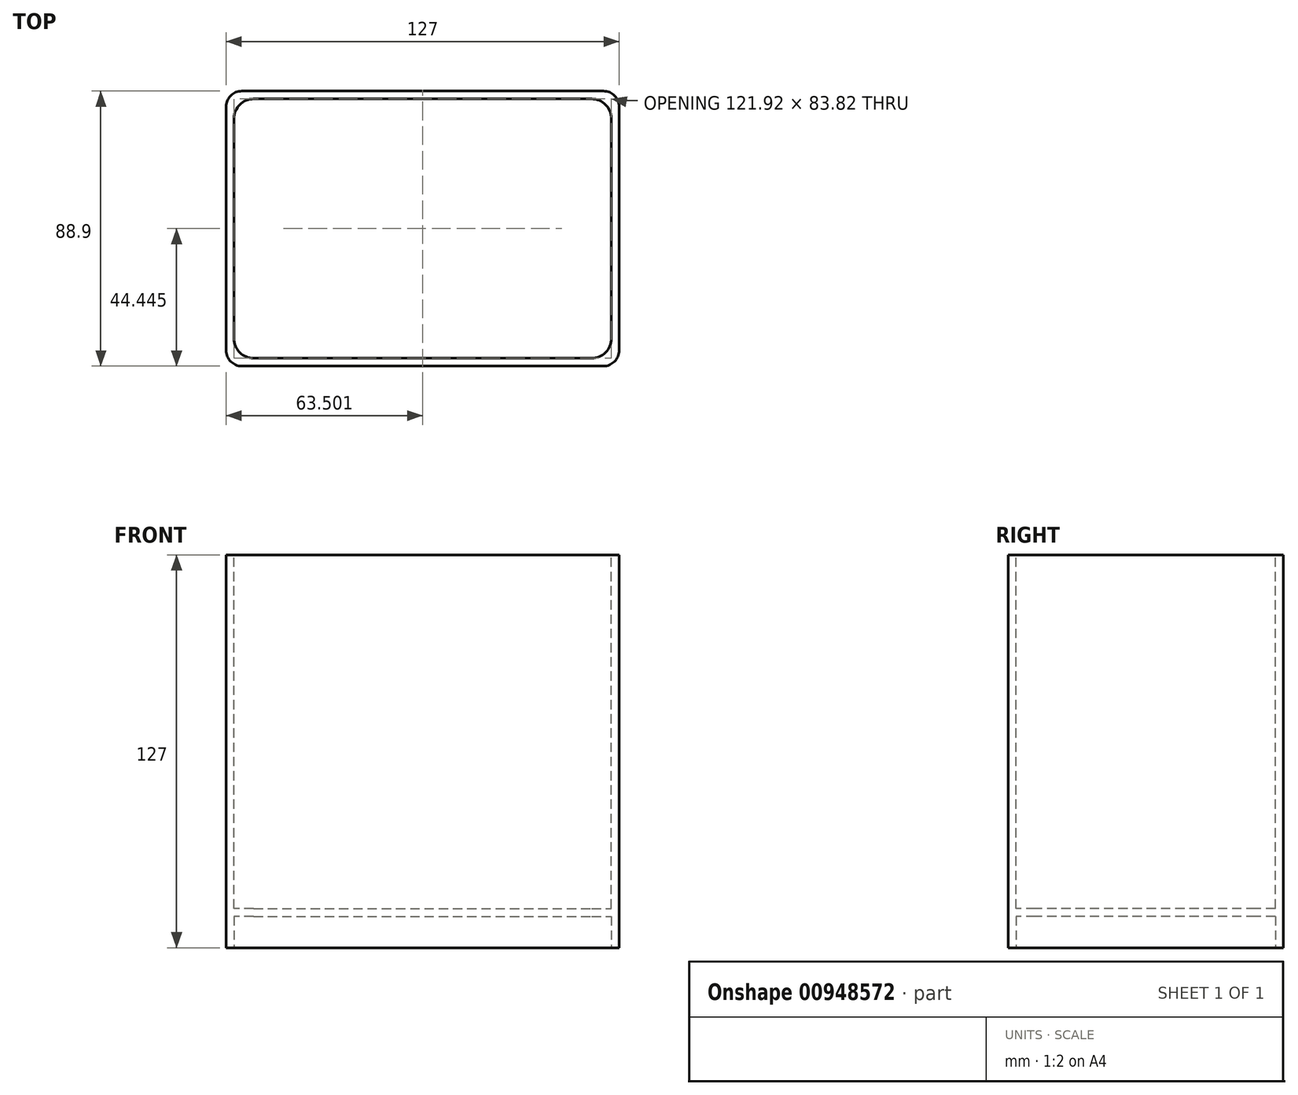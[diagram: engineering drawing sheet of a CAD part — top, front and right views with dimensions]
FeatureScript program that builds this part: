
annotation { "Feature Type Name" : "Feature", "Feature Type Description" : "" }
export const myFeature = defineFeature(function(context is Context, id is Id, definition is map)
    precondition{}
    {
        {
            var Q0;
            Q0=qCreatedBy(makeId("Top.planeOp"),FACE);
            var sketch = newSketch(context, id + "F0", { "sketchPlane" : qUnion([Q0])});
            skLineSegment(sketch, "E0.bottom", {"start": v(-59.26, 52.08) * mm, "end": v(67.74, 52.08) * mm});
            skLineSegment(sketch, "E0.top", {"start": v(-59.26, -36.82) * mm, "end": v(67.74, -36.82) * mm});
            skLineSegment(sketch, "E0.left", {"start": v(-59.26, 52.08) * mm, "end": v(-59.26, -36.82) * mm});
            skLineSegment(sketch, "E0.right", {"start": v(67.74, 52.08) * mm, "end": v(67.74, -36.82) * mm});
            skSolve(sketch);
        }
        {
            var Q0;
            Q0 = qSketchRegion(id + "F0", true);
            extrude(context, id + "F1", {"entities" : qUnion([Q0]), "depth" : 127 * mm, "offsetDistance" : 25.4 * mm});
        }
        {
            var Q0;
            Q0=makeQuery(id+"F1.opExtrude","SWEPT_EDGE",EDGE,{"disambiguationData":[OSD([sQuery(id+"F0.wireOp",EDGE,"E0.top"),sQuery(id+"F0.wireOp",EDGE,"E0.left")])]});
            var Q1;
            Q1=makeQuery(id+"F1.opExtrude","SWEPT_EDGE",EDGE,{"disambiguationData":[OSD([sQuery(id+"F0.wireOp",EDGE,"E0.top"),sQuery(id+"F0.wireOp",EDGE,"E0.right")])]});
            var Q2;
            Q2=makeQuery(id+"F1.opExtrude","SWEPT_EDGE",EDGE,{"disambiguationData":[OSD([sQuery(id+"F0.wireOp",EDGE,"E0.bottom"),sQuery(id+"F0.wireOp",EDGE,"E0.right")])]});
            var Q3;
            Q3=makeQuery(id+"F1.opExtrude","SWEPT_EDGE",EDGE,{"disambiguationData":[OSD([sQuery(id+"F0.wireOp",EDGE,"E0.bottom"),sQuery(id+"F0.wireOp",EDGE,"E0.left")])]});
            fillet(context, id + "F2", {"entities" : qUnion([Q0, Q1, Q2, Q3]), "radius" : 5.08 * mm, "tangentPropagation" : true, "allowEdgeOverflow" : false});
        }
        {
            var Q0;
            Q0=makeQuery(id+"F1.opExtrude","CAP_FACE",FACE,{"disambiguationData":[OSD([sQuery(id+"F0.wireOp",EDGE,"E0.bottom"),sQuery(id+"F0.wireOp",EDGE,"E0.top"),sQuery(id+"F0.wireOp",EDGE,"E0.left"),sQuery(id+"F0.wireOp",EDGE,"E0.right")])],"isStart":false});
            var sketch = newSketch(context, id + "F3", { "sketchPlane" : qUnion([Q0])});
            skLineSegment(sketch, "E1.0", {"start": v(-50.37, 49.54) * mm, "end": v(58.85, 49.54) * mm});
            skLineSegment(sketch, "E1.1", {"start": v(-56.72, 43.19) * mm, "end": v(-56.72, -27.93) * mm});
            skLineSegment(sketch, "E1.2", {"start": v(-50.37, -34.28) * mm, "end": v(58.85, -34.28) * mm});
            skLineSegment(sketch, "E1.3", {"start": v(65.2, 43.19) * mm, "end": v(65.2, -27.93) * mm});
            skPoint(sketch, "E2.visualSharp", {"position": v(-56.72, 49.54) * mm});
            skArc(sketch, "E2.filletArc", {"start": v(-50.37, 49.54) * mm, "mid": v(-54.86, 47.68) * mm, "end": v(-56.72, 43.19) * mm});
            skPoint(sketch, "E3.visualSharp", {"position": v(-56.72, -34.28) * mm});
            skArc(sketch, "E3.filletArc", {"start": v(-56.72, -27.93) * mm, "mid": v(-54.86, -32.43) * mm, "end": v(-50.37, -34.28) * mm});
            skPoint(sketch, "E4.visualSharp", {"position": v(65.2, 49.54) * mm});
            skArc(sketch, "E4.filletArc", {"start": v(65.2, 43.19) * mm, "mid": v(63.34, 47.68) * mm, "end": v(58.85, 49.54) * mm});
            skPoint(sketch, "E5.visualSharp", {"position": v(65.2, -34.28) * mm});
            skArc(sketch, "E5.filletArc", {"start": v(58.85, -34.28) * mm, "mid": v(63.34, -32.43) * mm, "end": v(65.2, -27.93) * mm});
            skSolve(sketch);
        }
        {
            var Q0;
            Q0=makeQuery(id+"F3.imprint","IMPRINT",FACE,{"disambiguationData":[TD([[makeQuery(id+"F3.imprint","IMPRINT",EDGE,{"derivedFrom":sQuery(id+"F3.wireOp",EDGE,"E1.0")}),-1.0]])]});
            extrude(context, id + "F4", {"entities" : qUnion([Q0]), "operationType" : NewBodyOperationType.REMOVE, "oppositeDirection" : true, "depth" : 114.3 * mm, "offsetDistance" : 25.4 * mm});
        }
        {
            var Q0;
            Q0=makeQuery(id+"F1.opExtrude","CAP_FACE",FACE,{"disambiguationData":[OSD([sQuery(id+"F0.wireOp",EDGE,"E0.bottom"),sQuery(id+"F0.wireOp",EDGE,"E0.top"),sQuery(id+"F0.wireOp",EDGE,"E0.left"),sQuery(id+"F0.wireOp",EDGE,"E0.right")])],"isStart":true});
            var sketch = newSketch(context, id + "F5", { "sketchPlane" : qUnion([Q0])});
            skLineSegment(sketch, "E6.0", {"start": v(65.2, -43.19) * mm, "end": v(65.2, 27.93) * mm});
            skArc(sketch, "E7.0", {"start": v(58.85, 34.28) * mm, "mid": v(63.34, 32.43) * mm, "end": v(65.2, 27.93) * mm});
            skLineSegment(sketch, "E8.0", {"start": v(-50.37, 34.28) * mm, "end": v(58.85, 34.28) * mm});
            skArc(sketch, "E9.0", {"start": v(-56.72, 27.93) * mm, "mid": v(-54.86, 32.43) * mm, "end": v(-50.37, 34.28) * mm});
            skLineSegment(sketch, "E10.0", {"start": v(-56.72, -43.19) * mm, "end": v(-56.72, 27.93) * mm});
            skArc(sketch, "E11.0", {"start": v(-50.37, -49.54) * mm, "mid": v(-54.86, -47.68) * mm, "end": v(-56.72, -43.19) * mm});
            skLineSegment(sketch, "E12.0", {"start": v(-50.37, -49.54) * mm, "end": v(58.85, -49.54) * mm});
            skArc(sketch, "E13.0", {"start": v(65.2, -43.19) * mm, "mid": v(63.34, -47.68) * mm, "end": v(58.85, -49.54) * mm});
            skSolve(sketch);
        }
        {
            var Q0;
            Q0=makeQuery(id+"F5.imprint","IMPRINT",FACE,{"disambiguationData":[TD([[makeQuery(id+"F5.imprint","IMPRINT",EDGE,{"derivedFrom":sQuery(id+"F5.wireOp",EDGE,"E6.0")}),1.0]])]});
            extrude(context, id + "F6", {"entities" : qUnion([Q0]), "operationType" : NewBodyOperationType.REMOVE, "oppositeDirection" : true, "depth" : 10.16 * mm, "offsetDistance" : 25.4 * mm});
        }
    });
